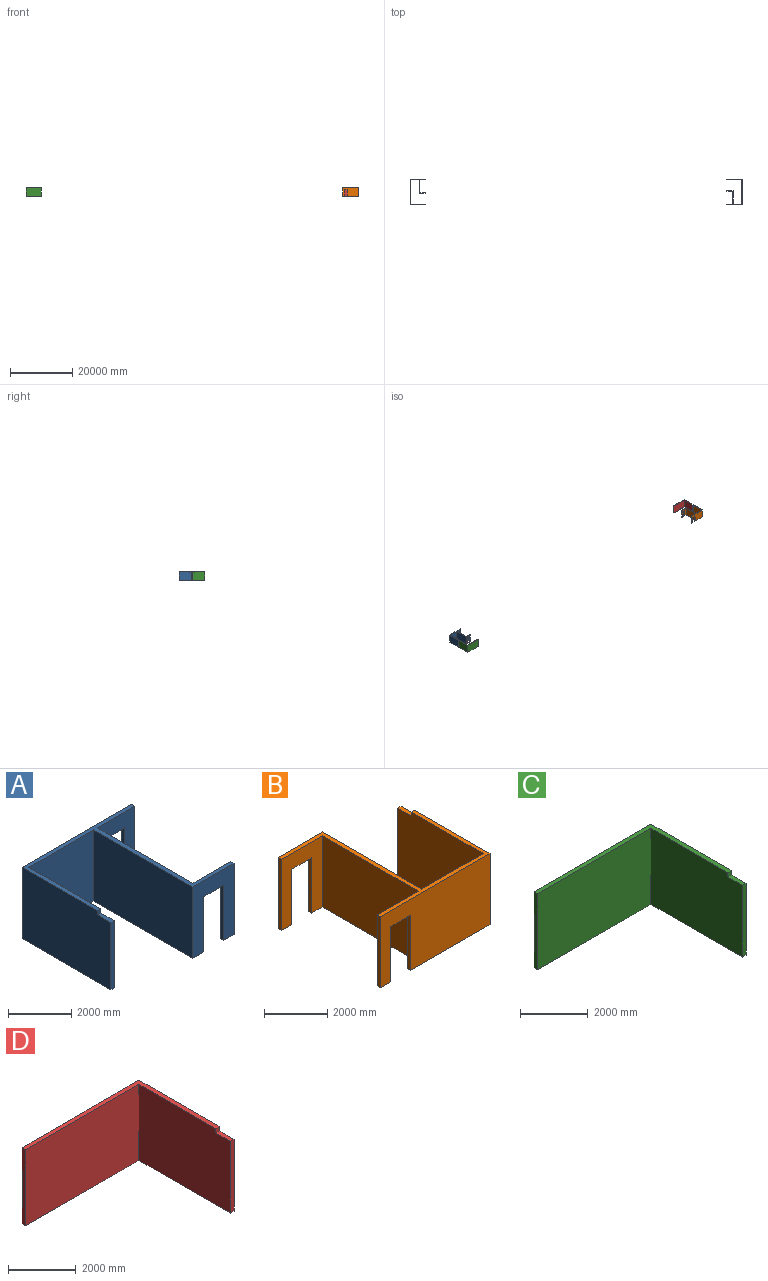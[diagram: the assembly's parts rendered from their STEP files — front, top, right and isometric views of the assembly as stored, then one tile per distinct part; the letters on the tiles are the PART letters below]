
ASSEMBLY  parts=4 mates=3
PART A: 24 faces, bbox 4876.8x4572x2743.2 mm
  f0: plane 4876.8x2743.2mm, normal (0,1,0), area 11481267.4mm2, adj f1,f6,f7,f11,f17,f18,f19,f20
  f1: plane 457.2x152.4mm, normal (0,0,-1), area 69677.3mm2, adj f0,f5,f17,f19
  f2: plane 457.2x152.4mm, normal (0,0,-1), area 69677.3mm2, adj f3,f4,f15,f22
  f3: plane 2743.2x1828.8mm, normal (0,-1,0), area 3119993.8mm2, adj f2,f7,f11,f14,f15,f21,f22,f23
  f4: plane 2743.2x1676.4mm, normal (0,1,0), area 2701930.1mm2, adj f2,f7,f11,f15,f16,f21,f22,f23
  f5: plane 2743.2x1676.4mm, normal (0,-1,0), area 2701930.1mm2, adj f1,f7,f11,f16,f17,f18,f19,f20
  f6: plane 3962.4x2743.2mm, normal (-1,0,0), area 10776752.6mm2, adj f0,f7,f10,f11,f12,f13
  f7: plane 4876.8x4572mm, normal (0,0,1), area 2159995.7mm2, adj f0,f3,f4,f5,f6,f8,f9,f13
  f8: plane 3810x2743.2mm, normal (1,0,0), area 10358689mm2, adj f7,f9,f10,f11,f12,f13
  f9: plane 2895.6x2743.2mm, normal (0,-1,0), area 7943209.9mm2, adj f7,f8,f11,f14
  f10: plane 2590.8x152.4mm, normal (0,-1,0), area 394837.9mm2, adj f6,f8,f11,f12
  f11: plane 4572x3530.6mm, normal (0,0,-1), area 1842577mm2, adj f0,f3,f4,f5,f6,f8,f9,f10
  f12: plane 609.6x152.4mm, normal (0,0,1), area 92903mm2, adj f6,f8,f10,f13
  f13: plane 152.4x152.4mm, normal (0,-1,0), area 23225.8mm2, adj f6,f7,f8,f12
  f14: plane 4419.6x2743.2mm, normal (-1,0,0), area 12123846.7mm2, adj f3,f7,f9,f11
  f15: plane 2743.2x152.4mm, normal (1,0,0), area 418063.7mm2, adj f2,f3,f4,f7
  f16: plane 4267.2x2743.2mm, normal (1,0,0), area 11705783mm2, adj f4,f5,f7,f11
  f17: plane 2743.2x152.4mm, normal (1,0,0), area 418063.7mm2, adj f0,f1,f5,f7
  f18: plane 889x152.4mm, normal (0,0,-1), area 135483.6mm2, adj f0,f5,f19,f20
  f19: plane 2133.6x152.4mm, normal (-1,0,0), area 325160.6mm2, adj f0,f1,f5,f18
  f20: plane 2133.6x152.4mm, normal (1,0,0), area 325160.6mm2, adj f0,f5,f11,f18
  f21: plane 2133.6x152.4mm, normal (1,0,0), area 325160.6mm2, adj f3,f4,f11,f23
  f22: plane 2133.6x152.4mm, normal (-1,0,0), area 325160.6mm2, adj f2,f3,f4,f23
  f23: plane 889x152.4mm, normal (0,0,-1), area 135483.6mm2, adj f3,f4,f21,f22
PART B: 24 faces, bbox 4876.8x4572x2743.2 mm
  f0: plane 4876.8x2743.2mm, normal (0,-1,0), area 11481267.4mm2, adj f1,f9,f11,f12,f17,f18,f19,f20
  f1: plane 457.2x152.4mm, normal (0,0,-1), area 69677.3mm2, adj f0,f5,f17,f20
  f2: plane 457.2x152.4mm, normal (0,0,-1), area 69677.3mm2, adj f3,f4,f16,f21
  f3: plane 2743.2x1981.2mm, normal (0,1,0), area 3538057.4mm2, adj f2,f11,f12,f15,f16,f21,f22,f23
  f4: plane 2743.2x1828.8mm, normal (0,-1,0), area 3119993.8mm2, adj f2,f6,f11,f12,f16,f21,f22,f23
  f5: plane 2743.2x1828.8mm, normal (0,1,0), area 3119993.8mm2, adj f1,f6,f11,f12,f17,f18,f19,f20
  f6: plane 4267.2x2743.2mm, normal (-1,0,0), area 11705783mm2, adj f4,f5,f11,f12
  f7: plane 2743.2x2743.2mm, normal (0,1,0), area 7525146.2mm2, adj f8,f11,f12,f15
  f8: plane 3810x2743.2mm, normal (-1,0,0), area 10358689mm2, adj f7,f10,f11,f12,f13,f14
  f9: plane 3962.4x2743.2mm, normal (1,0,0), area 10776752.6mm2, adj f0,f10,f11,f12,f13,f14
  f10: plane 2590.8x152.4mm, normal (0,1,0), area 394837.9mm2, adj f8,f9,f12,f13
  f11: plane 4876.8x4572mm, normal (0,0,1), area 2183221.4mm2, adj f0,f3,f4,f5,f6,f7,f8,f9
  f12: plane 4572x3530.6mm, normal (0,0,-1), area 1865802.7mm2, adj f0,f3,f4,f5,f6,f7,f8,f9
  f13: plane 609.6x152.4mm, normal (0,0,1), area 92903mm2, adj f8,f9,f10,f14
  f14: plane 152.4x152.4mm, normal (0,1,0), area 23225.8mm2, adj f8,f9,f11,f13
  f15: plane 4419.6x2743.2mm, normal (1,0,0), area 12123846.7mm2, adj f3,f7,f11,f12
  f16: plane 2743.2x152.4mm, normal (-1,0,0), area 418063.7mm2, adj f2,f3,f4,f11
  f17: plane 2743.2x152.4mm, normal (-1,0,0), area 418063.7mm2, adj f0,f1,f5,f11
  f18: plane 2133.6x152.4mm, normal (-1,0,0), area 325160.6mm2, adj f0,f5,f12,f19
  f19: plane 889x152.4mm, normal (0,0,-1), area 135483.6mm2, adj f0,f5,f18,f20
  f20: plane 2133.6x152.4mm, normal (1,0,0), area 325160.6mm2, adj f0,f1,f5,f19
  f21: plane 2133.6x152.4mm, normal (1,0,0), area 325160.6mm2, adj f2,f3,f4,f22
  f22: plane 889x152.4mm, normal (0,0,-1), area 135483.6mm2, adj f3,f4,f21,f23
  f23: plane 2133.6x152.4mm, normal (-1,0,0), area 325160.6mm2, adj f3,f4,f12,f22
PART C: 10 faces, bbox 4876.8x3962.4x2743.2 mm
  f0: plane 4876.8x3352.8mm, normal (0,0,1), area 1230965.3mm2, adj f1,f2,f3,f4,f6,f9
  f1: plane 4876.8x2743.2mm, normal (0,1,0), area 13378037.8mm2, adj f0,f2,f6,f7
  f2: plane 2743.2x152.4mm, normal (-1,0,0), area 418063.7mm2, adj f0,f1,f3,f7
  f3: plane 4724.4x2743.2mm, normal (0,-1,0), area 12959974.1mm2, adj f0,f2,f4,f7
  f4: plane 3810x2743.2mm, normal (-1,0,0), area 10358689mm2, adj f0,f3,f5,f7,f8,f9
  f5: plane 2590.8x152.4mm, normal (0,-1,0), area 394837.9mm2, adj f4,f6,f7,f8
  f6: plane 3962.4x2743.2mm, normal (1,0,0), area 10776752.6mm2, adj f0,f1,f5,f7,f8,f9
  f7: plane 4876.8x3962.4mm, normal (0,0,-1), area 1323868.3mm2, adj f1,f2,f3,f4,f5,f6
  f8: plane 609.6x152.4mm, normal (0,0,1), area 92903mm2, adj f4,f5,f6,f9
  f9: plane 152.4x152.4mm, normal (0,-1,0), area 23225.8mm2, adj f0,f4,f6,f8
PART D: 10 faces, bbox 4876.8x3962.4x2743.2 mm
  f0: plane 4876.8x3352.8mm, normal (0,0,1), area 1230965.3mm2, adj f1,f2,f3,f4,f6,f9
  f1: plane 4876.8x2743.2mm, normal (0,1,0), area 13378037.8mm2, adj f0,f2,f6,f7
  f2: plane 2743.2x152.4mm, normal (-1,0,0), area 418063.7mm2, adj f0,f1,f3,f7
  f3: plane 4724.4x2743.2mm, normal (0,-1,0), area 12959974.1mm2, adj f0,f2,f4,f7
  f4: plane 3810x2743.2mm, normal (-1,0,0), area 10358689mm2, adj f0,f3,f5,f7,f8,f9
  f5: plane 2590.8x152.4mm, normal (0,-1,0), area 394837.9mm2, adj f4,f6,f7,f8
  f6: plane 3962.4x2743.2mm, normal (1,0,0), area 10776752.6mm2, adj f0,f1,f5,f7,f8,f9
  f7: plane 4876.8x3962.4mm, normal (0,0,-1), area 1323868.3mm2, adj f1,f2,f3,f4,f5,f6
  f8: plane 609.6x152.4mm, normal (0,0,1), area 92903mm2, adj f4,f5,f6,f9
  f9: plane 152.4x152.4mm, normal (0,-1,0), area 23225.8mm2, adj f0,f4,f6,f8
PLACE A t=(-106832.4,-152.4,0)mm
PLACE B t=(0,-8229.6,0)mm
PLACE C rot(axis=(0,0,1),180deg) t=(-106984.8,-8229.6,0)mm
PLACE D at identity
MATE fastened A.f7 <-> D.f0  axis (0,0,1) through (-103936.8,-152.4,2743.2)mm
MATE fastened C.f0 <-> A.f7  axis (0,0,1) through (-102108,-8229.6,2743.2)mm
MATE fastened B.f11 <-> D.f0  axis (0,0,1) through (-3048,-8229.6,2743.2)mm
